# Revit family: Video_Conferencing-Camera-Vaddio-Venture_VideoBAR_Series--
name_source: partatom
category: Specialty Equipment
units: mm (PartAtom-declared; Revit-internal decimal feet)

## family parameters
Cut with Voids When Loaded = No
Host = Face
Maintain Annotation Orientation = No
OmniClass Number = 23.40.70.14.57
OmniClass Title = Office Equipment and Furnishings
Part Type = Normal
Room Calculation Point = No
Round Connector Dimension = Use Diameter
Shared = No

## types (1)
- Standard
    Apparent Power = 24 VA
    Bottom Case Material = Plastic - Legrand Venture - Black
    Date Modified = July 5, 2024
    Default Elevation = 4' - 0"
    Description = See Part Description
    ENGworks Global = https://engworksglobal.com
    Family Version = 1.0
    Full Load Amps = 2 A
    Manufacturer = Vaddio
    Maximum Operating Temperature = 104 °F
    Minimum Operating Temperature = 32 °F
    Model = See Part Number
    Model Disclaimer = Contact Vaddio For More Information
    Number of Poles = 1
    Part Number = 999-50909-000
    Power Factor = 1
    Product Page URL = https://www.legrandav.com
    Series = Venture® VideoBAR
    Top Case Material = Plastic - Legrand Venture - Teal
    URL = https://www.legrandav.com
    Unit Weight = 7.35 lb
    Voltage = 12 V

## geometry (parser evidence)
native form markers: Sweep x8
no freeform markers — native parametric forms only
